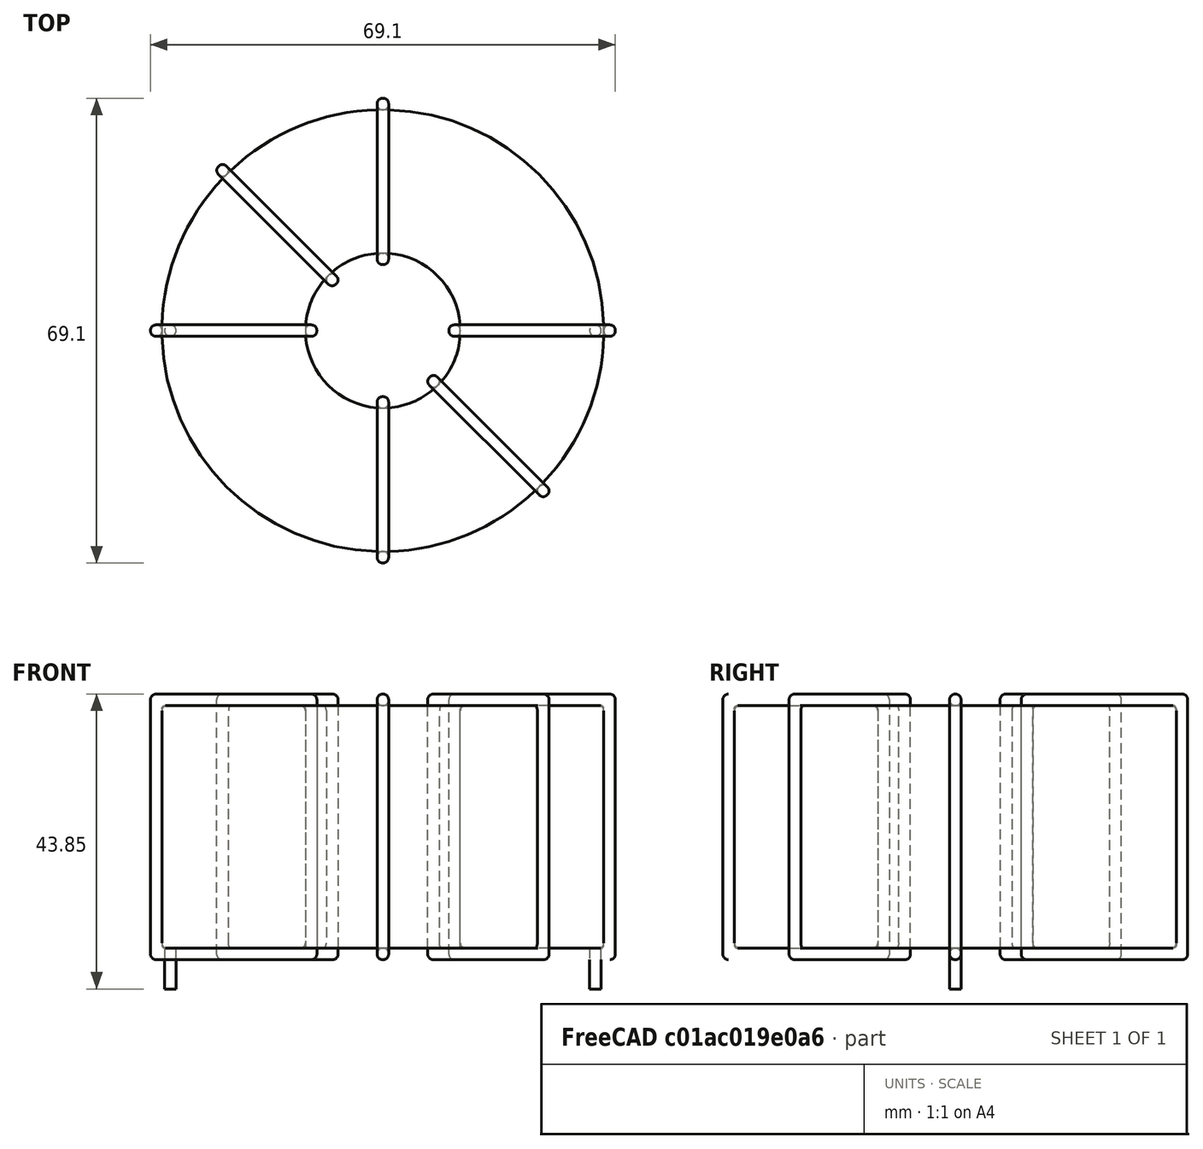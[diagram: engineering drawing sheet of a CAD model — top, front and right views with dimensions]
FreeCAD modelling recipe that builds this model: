
FCSTD DOCUMENT  (FreeCAD 0.16R6703 (Git))
Label: L_Toroid_Horizontal_D69.1mm_P63.20mm_Vishay_TJ9
License: All rights reserved
LicenseURL: http://en.wikipedia.org/wiki/All_rights_reserved
objects: Sketcher::SketchObject×6, PartDesign::Pad×6, PartDesign::Fillet×5, Spreadsheet::Sheet×1
note: 23 computed .brp shape members not serialized (recipe doc carries the construction recipe); baked Part::Feature solids carry a one-line shape summary decoded from their .brp

FEATURE [Spreadsheet::Sheet] Spreadsheet  label="dimensions"
  cells = A1=Wx; B1(Wx)=69.09999999999999; C1(WW)=23.03333333333333; D1=69.09999999999999; A2=Wy; B2(Wy)=69.09999999999999; D2=69.09999999999999; A3=RM; B3(RMx)=63.2; C3(RMy)=0; A4=d_wire; B4(d_wire)=1.7; A5=H; B5(H)=36.1; A6=offsetx; B6(offsetx)=2.949999999999996
FEATURE [Sketcher::SketchObject] Sketch
  Placement = pos=(0,0,2.2) rot=(0,0,1;0rad)
  expr: Placement.Base.z = 0.5 + Spreadsheet.d_wire
  expr: Constraints[0] = Spreadsheet.Wx / 2 - Spreadsheet.d_wire
  expr: Constraints[4] = Spreadsheet.WW / 2
  expr: Constraints[2] = Spreadsheet.RMy / 2
  expr: Constraints[1] = Spreadsheet.RMx / 2
  sketch-geometry (2):
    g0: Circle CenterX=31.6 CenterY=0 CenterZ=0 NormalX=0 NormalY=0 NormalZ=1 Radius=32.85
    g1: Circle CenterX=31.6 CenterY=0 CenterZ=0 NormalX=0 NormalY=0 NormalZ=1 Radius=11.5167
  constraints (5):
    c: Radius(g0) = 32.85
    c: DistanceX(g-1,g0) = 31.6
    c: DistanceY(g-1,g0) = 0
    c: Coincident(g1,g0)
    c: Radius(g1) = 11.5167
FEATURE [PartDesign::Pad] Pad
  Length = 36.1
  Length2 = 100
  Placement = pos=(0,0,2.2) rot=(0,0,1;0rad)
  Sketch = -> Sketch
  Type = 0
  expr: Length = Spreadsheet.H
FEATURE [Sketcher::SketchObject] Sketch001
  Placement = pos=(0,0,1.35) rot=(0,0,1;0rad)
  expr: Placement.Base.z = 0.5 + Spreadsheet.d_wire * 0.5
  expr: Constraints[4] = Spreadsheet.RMx
  expr: Constraints[2] = Spreadsheet.RMy
  expr: Constraints[1] = Spreadsheet.d_wire / 2
  sketch-geometry (2):
    g0: Circle CenterX=0 CenterY=0 CenterZ=0 NormalX=0 NormalY=0 NormalZ=1 Radius=0.85
    g1: Circle CenterX=63.2 CenterY=0 CenterZ=0 NormalX=0 NormalY=0 NormalZ=1 Radius=0.85
  constraints (5):
    c: Equal(g0,g1)
    c: Radius(g0) = 0.85
    c: DistanceY(g-1,g1) = 0
    c: Coincident(g0,g-1)
    c: DistanceX(g-1,g1) = 63.2
FEATURE [PartDesign::Pad] Pad001
  Length = 0.85
  Length2 = 5.2
  Placement = pos=(0,0,1.35) rot=(0,0,1;0rad)
  Reversed = true
  Sketch = -> Sketch001
  Type = 4
  expr: Length2 = 3.5 + Spreadsheet.d_wire
  expr: Length = Spreadsheet.d_wire / 2
FEATURE [PartDesign::Fillet] Fillet
  Base = -> Pad [Edge6,Edge3,Edge2]
  Placement = pos=(0,0,2.2) rot=(0,0,1;0rad)
  Radius = 0.5
FEATURE [Sketcher::SketchObject] Sketch003
  Placement = pos=(31.6,0,0) rot=(1,0,0;1.5708rad)
  expr: Placement.Base.x = Spreadsheet.RMx / 2
  expr: Constraints[49] = Spreadsheet.Wx - Spreadsheet.d_wire * 2
  expr: Constraints[44] = Spreadsheet.d_wire
  expr: Constraints[23] = Spreadsheet.H
  expr: Constraints[22] = Spreadsheet.Wx / 2 - Spreadsheet.d_wire
  expr: Placement.Base.y = Spreadsheet.RMy / 2
  expr: Constraints[21] = (Spreadsheet.Wx - Spreadsheet.WW) / 2 - Spreadsheet.d_wire
  expr: Constraints[19] = Spreadsheet.d_wire
  expr: Constraints[17] = Spreadsheet.d_wire
  expr: Constraints[18] = Spreadsheet.d_wire
  expr: Constraints[16] = Spreadsheet.d_wire
  sketch-geometry (16):
    g0: LineSegment StartX=-9.81667 StartY=0.5 StartZ=0 EndX=-34.55 EndY=0.5 EndZ=0
    g1: LineSegment StartX=-34.55 StartY=0.5 StartZ=0 EndX=-34.55 EndY=40 EndZ=0
    g2: LineSegment StartX=-34.55 StartY=40 StartZ=0 EndX=-9.81667 EndY=40 EndZ=0
    g3: LineSegment StartX=-9.81667 StartY=40 StartZ=0 EndX=-9.81667 EndY=0.5 EndZ=0
    g4: LineSegment StartX=-32.85 StartY=38.3 StartZ=0 EndX=-11.5167 EndY=38.3 EndZ=0
    g5: LineSegment StartX=-11.5167 StartY=38.3 StartZ=0 EndX=-11.5167 EndY=2.2 EndZ=0
    g6: LineSegment StartX=-11.5167 StartY=2.2 StartZ=0 EndX=-32.85 EndY=2.2 EndZ=0
    g7: LineSegment StartX=-32.85 StartY=2.2 StartZ=0 EndX=-32.85 EndY=38.3 EndZ=0
    g8: LineSegment StartX=9.81667 StartY=40 StartZ=0 EndX=34.55 EndY=40 EndZ=0
    g9: LineSegment StartX=34.55 StartY=40 StartZ=0 EndX=34.55 EndY=0.5 EndZ=0
    g10: LineSegment StartX=34.55 StartY=0.5 StartZ=0 EndX=9.81667 EndY=0.5 EndZ=0
    g11: LineSegment StartX=9.81667 StartY=0.5 StartZ=0 EndX=9.81667 EndY=40 EndZ=0
    g12: LineSegment StartX=11.5167 StartY=38.3 StartZ=0 EndX=32.85 EndY=38.3 EndZ=0
    g13: LineSegment StartX=32.85 StartY=38.3 StartZ=0 EndX=32.85 EndY=2.2 EndZ=0
    g14: LineSegment StartX=32.85 StartY=2.2 StartZ=0 EndX=11.5167 EndY=2.2 EndZ=0
    g15: LineSegment StartX=11.5167 StartY=2.2 StartZ=0 EndX=11.5167 EndY=38.3 EndZ=0
  constraints (50):
    c: Horizontal(g0)
    c: Coincident(g1,g0)
    c: Vertical(g1)
    c: Coincident(g2,g1)
    c: Horizontal(g2)
    c: Coincident(g3,g2)
    c: Coincident(g3,g0)
    c: Vertical(g3)
    c: Coincident(g4,g5)
    c: Coincident(g5,g6)
    c: Coincident(g6,g7)
    c: Coincident(g7,g4)
    c: Horizontal(g4)
    c: Horizontal(g6)
    c: Vertical(g5)
    c: Vertical(g7)
    c: DistanceX(g1,g4) = 1.7
    c: DistanceY(g4,g1) = 1.7
    c: DistanceX(g5,g0) = 1.7
    c: DistanceY(g0,g5) = 1.7
    c: DistanceY(g-1,g0) = 0.5
    c: DistanceX(g6,g6) = 21.3333
    c: DistanceX(g6,g-1) = 32.85
    c: DistanceY(g7,g7) = 36.1
    c: Coincident(g8,g9)
    c: Coincident(g9,g10)
    c: Coincident(g10,g11)
    c: Coincident(g11,g8)
    c: Horizontal(g8)
    c: Horizontal(g10)
    c: Vertical(g9)
    c: Vertical(g11)
    c: Coincident(g12,g13)
    c: Coincident(g13,g14)
    c: Coincident(g14,g15)
    c: Coincident(g15,g12)
    c: Horizontal(g12)
    c: Horizontal(g14)
    c: Vertical(g13)
    c: Vertical(g15)
    c: DistanceY(g8,g2) = 0
    c: DistanceY(g10,g0) = 0
    c: DistanceY(g14,g5) = 0
    c: DistanceY(g12,g4) = 0
    c: DistanceX(g8,g12) = 1.7
    c: Equal(g8,g2)
    c: Equal(g12,g4)
    c: Equal(g9,g1)
    c: Equal(g13,g7)
    c: DistanceX(g4,g12) = 65.7
FEATURE [PartDesign::Pad] Pad002
  Length = 1.7
  Length2 = 100
  Midplane = true
  Placement = pos=(31.6,0,0) rot=(1,0,0;1.5708rad)
  Sketch = -> Sketch003
  Type = 0
  expr: Length = Spreadsheet.d_wire
FEATURE [PartDesign::Fillet] Fillet001
  Base = -> Pad002 [Edge38,Edge41,Edge42,Edge43,Edge29,Edge32,Edge33,Edge34,Edge25,Edge35,Edge36,Edge13,Edge14,Edge15,Edge16,Edge17,Edge18,Edge19,Edge1,Edge2,Edge3,Edge4,Edge5,Edge6,Edge7,Edge37,Edge39,Edge40,Edge20,Edge23,Edge24,Edge21,Edge22,Edge8,Edge9,Edge10,Edge11,Edge12,Edge26,Edge27,+8 more]
  Placement = pos=(31.6,0,0) rot=(1,0,0;1.5708rad)
  Radius = 0.799
  expr: Radius = Spreadsheet.d_wire * 0.47
FEATURE [Sketcher::SketchObject] Sketch004
  Placement = pos=(31.6,0,0) rot=(0.862856,0.357407,0.357407;1.71777rad)
  expr: Placement.Base.x = Spreadsheet.RMx / 2
  expr: Constraints[49] = Spreadsheet.Wx - 2 * Spreadsheet.d_wire
  expr: Constraints[44] = Spreadsheet.d_wire
  expr: Constraints[23] = Spreadsheet.H
  expr: Constraints[22] = Spreadsheet.Wx / 2 - Spreadsheet.d_wire
  expr: Placement.Base.y = Spreadsheet.RMy / 2
  expr: Constraints[21] = (Spreadsheet.Wx - Spreadsheet.WW) / 2 - Spreadsheet.d_wire
  expr: Constraints[19] = Spreadsheet.d_wire
  expr: Constraints[17] = Spreadsheet.d_wire
  expr: Constraints[18] = Spreadsheet.d_wire
  expr: Constraints[16] = Spreadsheet.d_wire
  sketch-geometry (16):
    g0: LineSegment StartX=-9.81667 StartY=0.5 StartZ=0 EndX=-34.55 EndY=0.5 EndZ=0
    g1: LineSegment StartX=-34.55 StartY=0.5 StartZ=0 EndX=-34.55 EndY=40 EndZ=0
    g2: LineSegment StartX=-34.55 StartY=40 StartZ=0 EndX=-9.81667 EndY=40 EndZ=0
    g3: LineSegment StartX=-9.81667 StartY=40 StartZ=0 EndX=-9.81667 EndY=0.5 EndZ=0
    g4: LineSegment StartX=-32.85 StartY=38.3 StartZ=0 EndX=-11.5167 EndY=38.3 EndZ=0
    g5: LineSegment StartX=-11.5167 StartY=38.3 StartZ=0 EndX=-11.5167 EndY=2.2 EndZ=0
    g6: LineSegment StartX=-11.5167 StartY=2.2 StartZ=0 EndX=-32.85 EndY=2.2 EndZ=0
    g7: LineSegment StartX=-32.85 StartY=2.2 StartZ=0 EndX=-32.85 EndY=38.3 EndZ=0
    g8: LineSegment StartX=9.81667 StartY=40 StartZ=0 EndX=34.55 EndY=40 EndZ=0
    g9: LineSegment StartX=34.55 StartY=40 StartZ=0 EndX=34.55 EndY=0.5 EndZ=0
    g10: LineSegment StartX=34.55 StartY=0.5 StartZ=0 EndX=9.81667 EndY=0.5 EndZ=0
    g11: LineSegment StartX=9.81667 StartY=0.5 StartZ=0 EndX=9.81667 EndY=40 EndZ=0
    g12: LineSegment StartX=11.5167 StartY=38.3 StartZ=0 EndX=32.85 EndY=38.3 EndZ=0
    g13: LineSegment StartX=32.85 StartY=38.3 StartZ=0 EndX=32.85 EndY=2.2 EndZ=0
    g14: LineSegment StartX=32.85 StartY=2.2 StartZ=0 EndX=11.5167 EndY=2.2 EndZ=0
    g15: LineSegment StartX=11.5167 StartY=2.2 StartZ=0 EndX=11.5167 EndY=38.3 EndZ=0
  constraints (50):
    c: Horizontal(g0)
    c: Coincident(g1,g0)
    c: Vertical(g1)
    c: Coincident(g2,g1)
    c: Horizontal(g2)
    c: Coincident(g3,g2)
    c: Coincident(g3,g0)
    c: Vertical(g3)
    c: Coincident(g4,g5)
    c: Coincident(g5,g6)
    c: Coincident(g6,g7)
    c: Coincident(g7,g4)
    c: Horizontal(g4)
    c: Horizontal(g6)
    c: Vertical(g5)
    c: Vertical(g7)
    c: DistanceX(g1,g4) = 1.7
    c: DistanceY(g4,g1) = 1.7
    c: DistanceX(g5,g0) = 1.7
    c: DistanceY(g0,g5) = 1.7
    c: DistanceY(g-1,g0) = 0.5
    c: DistanceX(g6,g6) = 21.3333
    c: DistanceX(g6,g-1) = 32.85
    c: DistanceY(g7,g7) = 36.1
    c: Coincident(g8,g9)
    c: Coincident(g9,g10)
    c: Coincident(g10,g11)
    c: Coincident(g11,g8)
    c: Horizontal(g8)
    c: Horizontal(g10)
    c: Vertical(g9)
    c: Vertical(g11)
    c: Coincident(g12,g13)
    c: Coincident(g13,g14)
    c: Coincident(g14,g15)
    c: Coincident(g15,g12)
    c: Horizontal(g12)
    c: Horizontal(g14)
    c: Vertical(g13)
    c: Vertical(g15)
    c: DistanceY(g8,g2) = 0
    c: DistanceY(g10,g0) = 0
    c: DistanceY(g14,g5) = 0
    c: DistanceY(g12,g4) = 0
    c: DistanceX(g8,g12) = 1.7
    c: Equal(g8,g2)
    c: Equal(g12,g4)
    c: Equal(g9,g1)
    c: Equal(g13,g7)
    c: DistanceX(g4,g12) = 65.7
FEATURE [PartDesign::Pad] Pad003
  Length = 1.7
  Length2 = 100
  Midplane = true
  Placement = pos=(31.6,0,0) rot=(0.862856,0.357407,0.357407;1.71777rad)
  Sketch = -> Sketch004
  Type = 0
  expr: Length = Spreadsheet.d_wire
FEATURE [PartDesign::Fillet] Fillet002
  Base = -> Pad003 [Edge38,Edge41,Edge42,Edge43,Edge29,Edge32,Edge33,Edge34,Edge25,Edge35,Edge36,Edge13,Edge14,Edge15,Edge16,Edge17,Edge18,Edge19,Edge1,Edge2,Edge3,Edge4,Edge5,Edge6,Edge7,Edge37,Edge39,Edge40,Edge20,Edge23,Edge24,Edge21,Edge22,Edge8,Edge9,Edge10,Edge11,Edge12,Edge26,Edge27,+8 more]
  Placement = pos=(31.6,0,0) rot=(0.862856,0.357407,0.357407;1.71777rad)
  Radius = 0.799
  expr: Radius = Spreadsheet.d_wire * 0.47
FEATURE [Sketcher::SketchObject] Sketch005
  Placement = pos=(31.6,0,0) rot=(0.862856,-0.357407,-0.357407;1.71777rad)
  expr: Placement.Base.x = Spreadsheet.RMx / 2
  expr: Constraints[49] = Spreadsheet.Wx - 2 * Spreadsheet.d_wire
  expr: Constraints[44] = Spreadsheet.d_wire
  expr: Constraints[23] = Spreadsheet.H
  expr: Constraints[22] = Spreadsheet.Wx / 2 - Spreadsheet.d_wire
  expr: Placement.Base.y = Spreadsheet.RMy / 2
  expr: Constraints[21] = (Spreadsheet.Wx - Spreadsheet.WW) / 2 - Spreadsheet.d_wire
  expr: Constraints[19] = Spreadsheet.d_wire
  expr: Constraints[17] = Spreadsheet.d_wire
  expr: Constraints[18] = Spreadsheet.d_wire
  expr: Constraints[16] = Spreadsheet.d_wire
  sketch-geometry (16):
    g0: LineSegment StartX=-9.81667 StartY=0.5 StartZ=0 EndX=-34.55 EndY=0.5 EndZ=0
    g1: LineSegment StartX=-34.55 StartY=0.5 StartZ=0 EndX=-34.55 EndY=40 EndZ=0
    g2: LineSegment StartX=-34.55 StartY=40 StartZ=0 EndX=-9.81667 EndY=40 EndZ=0
    g3: LineSegment StartX=-9.81667 StartY=40 StartZ=0 EndX=-9.81667 EndY=0.5 EndZ=0
    g4: LineSegment StartX=-32.85 StartY=38.3 StartZ=0 EndX=-11.5167 EndY=38.3 EndZ=0
    g5: LineSegment StartX=-11.5167 StartY=38.3 StartZ=0 EndX=-11.5167 EndY=2.2 EndZ=0
    g6: LineSegment StartX=-11.5167 StartY=2.2 StartZ=0 EndX=-32.85 EndY=2.2 EndZ=0
    g7: LineSegment StartX=-32.85 StartY=2.2 StartZ=0 EndX=-32.85 EndY=38.3 EndZ=0
    g8: LineSegment StartX=9.81667 StartY=40 StartZ=0 EndX=34.55 EndY=40 EndZ=0
    g9: LineSegment StartX=34.55 StartY=40 StartZ=0 EndX=34.55 EndY=0.5 EndZ=0
    g10: LineSegment StartX=34.55 StartY=0.5 StartZ=0 EndX=9.81667 EndY=0.5 EndZ=0
    g11: LineSegment StartX=9.81667 StartY=0.5 StartZ=0 EndX=9.81667 EndY=40 EndZ=0
    g12: LineSegment StartX=11.5167 StartY=38.3 StartZ=0 EndX=32.85 EndY=38.3 EndZ=0
    g13: LineSegment StartX=32.85 StartY=38.3 StartZ=0 EndX=32.85 EndY=2.2 EndZ=0
    g14: LineSegment StartX=32.85 StartY=2.2 StartZ=0 EndX=11.5167 EndY=2.2 EndZ=0
    g15: LineSegment StartX=11.5167 StartY=2.2 StartZ=0 EndX=11.5167 EndY=38.3 EndZ=0
  constraints (50):
    c: Horizontal(g0)
    c: Coincident(g1,g0)
    c: Vertical(g1)
    c: Coincident(g2,g1)
    c: Horizontal(g2)
    c: Coincident(g3,g2)
    c: Coincident(g3,g0)
    c: Vertical(g3)
    c: Coincident(g4,g5)
    c: Coincident(g5,g6)
    c: Coincident(g6,g7)
    c: Coincident(g7,g4)
    c: Horizontal(g4)
    c: Horizontal(g6)
    c: Vertical(g5)
    c: Vertical(g7)
    c: DistanceX(g1,g4) = 1.7
    c: DistanceY(g4,g1) = 1.7
    c: DistanceX(g5,g0) = 1.7
    c: DistanceY(g0,g5) = 1.7
    c: DistanceY(g-1,g0) = 0.5
    c: DistanceX(g6,g6) = 21.3333
    c: DistanceX(g6,g-1) = 32.85
    c: DistanceY(g7,g7) = 36.1
    c: Coincident(g8,g9)
    c: Coincident(g9,g10)
    c: Coincident(g10,g11)
    c: Coincident(g11,g8)
    c: Horizontal(g8)
    c: Horizontal(g10)
    c: Vertical(g9)
    c: Vertical(g11)
    c: Coincident(g12,g13)
    c: Coincident(g13,g14)
    c: Coincident(g14,g15)
    c: Coincident(g15,g12)
    c: Horizontal(g12)
    c: Horizontal(g14)
    c: Vertical(g13)
    c: Vertical(g15)
    c: DistanceY(g8,g2) = 0
    c: DistanceY(g10,g0) = 0
    c: DistanceY(g14,g5) = 0
    c: DistanceY(g12,g4) = 0
    c: DistanceX(g8,g12) = 1.7
    c: Equal(g8,g2)
    c: Equal(g12,g4)
    c: Equal(g9,g1)
    c: Equal(g13,g7)
    c: DistanceX(g4,g12) = 65.7
FEATURE [PartDesign::Pad] Pad004
  Length = 1.7
  Length2 = 100
  Midplane = true
  Placement = pos=(31.6,0,0) rot=(0.862856,-0.357407,-0.357407;1.71777rad)
  Sketch = -> Sketch005
  Type = 0
  expr: Length = Spreadsheet.d_wire
FEATURE [PartDesign::Fillet] Fillet003
  Base = -> Pad004 [Edge38,Edge41,Edge42,Edge43,Edge29,Edge32,Edge33,Edge34,Edge25,Edge35,Edge36,Edge13,Edge14,Edge15,Edge16,Edge17,Edge18,Edge19,Edge1,Edge2,Edge3,Edge4,Edge5,Edge6,Edge7,Edge37,Edge39,Edge40,Edge20,Edge23,Edge24,Edge21,Edge22,Edge8,Edge9,Edge10,Edge11,Edge12,Edge26,Edge27,+8 more]
  Placement = pos=(31.6,0,0) rot=(0.862856,-0.357407,-0.357407;1.71777rad)
  Radius = 0.799
  expr: Radius = Spreadsheet.d_wire * 0.47
FEATURE [Sketcher::SketchObject] Sketch006
  Placement = pos=(31.6,0,0) rot=(0.57735,0.57735,0.57735;2.0944rad)
  expr: Placement.Base.x = Spreadsheet.RMx / 2
  expr: Constraints[49] = Spreadsheet.Wx - Spreadsheet.d_wire * 2
  expr: Constraints[44] = Spreadsheet.d_wire
  expr: Constraints[23] = Spreadsheet.H
  expr: Constraints[22] = Spreadsheet.Wx / 2 - Spreadsheet.d_wire
  expr: Placement.Base.y = Spreadsheet.RMy / 2
  expr: Constraints[21] = (Spreadsheet.Wx - Spreadsheet.WW) / 2 - Spreadsheet.d_wire
  expr: Constraints[19] = Spreadsheet.d_wire
  expr: Constraints[17] = Spreadsheet.d_wire
  expr: Constraints[18] = Spreadsheet.d_wire
  expr: Constraints[16] = Spreadsheet.d_wire
  sketch-geometry (16):
    g0: LineSegment StartX=-9.81667 StartY=0.5 StartZ=0 EndX=-34.55 EndY=0.5 EndZ=0
    g1: LineSegment StartX=-34.55 StartY=0.5 StartZ=0 EndX=-34.55 EndY=40 EndZ=0
    g2: LineSegment StartX=-34.55 StartY=40 StartZ=0 EndX=-9.81667 EndY=40 EndZ=0
    g3: LineSegment StartX=-9.81667 StartY=40 StartZ=0 EndX=-9.81667 EndY=0.5 EndZ=0
    g4: LineSegment StartX=-32.85 StartY=38.3 StartZ=0 EndX=-11.5167 EndY=38.3 EndZ=0
    g5: LineSegment StartX=-11.5167 StartY=38.3 StartZ=0 EndX=-11.5167 EndY=2.2 EndZ=0
    g6: LineSegment StartX=-11.5167 StartY=2.2 StartZ=0 EndX=-32.85 EndY=2.2 EndZ=0
    g7: LineSegment StartX=-32.85 StartY=2.2 StartZ=0 EndX=-32.85 EndY=38.3 EndZ=0
    g8: LineSegment StartX=9.81667 StartY=40 StartZ=0 EndX=34.55 EndY=40 EndZ=0
    g9: LineSegment StartX=34.55 StartY=40 StartZ=0 EndX=34.55 EndY=0.5 EndZ=0
    g10: LineSegment StartX=34.55 StartY=0.5 StartZ=0 EndX=9.81667 EndY=0.5 EndZ=0
    g11: LineSegment StartX=9.81667 StartY=0.5 StartZ=0 EndX=9.81667 EndY=40 EndZ=0
    g12: LineSegment StartX=11.5167 StartY=38.3 StartZ=0 EndX=32.85 EndY=38.3 EndZ=0
    g13: LineSegment StartX=32.85 StartY=38.3 StartZ=0 EndX=32.85 EndY=2.2 EndZ=0
    g14: LineSegment StartX=32.85 StartY=2.2 StartZ=0 EndX=11.5167 EndY=2.2 EndZ=0
    g15: LineSegment StartX=11.5167 StartY=2.2 StartZ=0 EndX=11.5167 EndY=38.3 EndZ=0
  constraints (50):
    c: Horizontal(g0)
    c: Coincident(g1,g0)
    c: Vertical(g1)
    c: Coincident(g2,g1)
    c: Horizontal(g2)
    c: Coincident(g3,g2)
    c: Coincident(g3,g0)
    c: Vertical(g3)
    c: Coincident(g4,g5)
    c: Coincident(g5,g6)
    c: Coincident(g6,g7)
    c: Coincident(g7,g4)
    c: Horizontal(g4)
    c: Horizontal(g6)
    c: Vertical(g5)
    c: Vertical(g7)
    c: DistanceX(g1,g4) = 1.7
    c: DistanceY(g4,g1) = 1.7
    c: DistanceX(g5,g0) = 1.7
    c: DistanceY(g0,g5) = 1.7
    c: DistanceY(g-1,g0) = 0.5
    c: DistanceX(g6,g6) = 21.3333
    c: DistanceX(g6,g-1) = 32.85
    c: DistanceY(g7,g7) = 36.1
    c: Coincident(g8,g9)
    c: Coincident(g9,g10)
    c: Coincident(g10,g11)
    c: Coincident(g11,g8)
    c: Horizontal(g8)
    c: Horizontal(g10)
    c: Vertical(g9)
    c: Vertical(g11)
    c: Coincident(g12,g13)
    c: Coincident(g13,g14)
    c: Coincident(g14,g15)
    c: Coincident(g15,g12)
    c: Horizontal(g12)
    c: Horizontal(g14)
    c: Vertical(g13)
    c: Vertical(g15)
    c: DistanceY(g8,g2) = 0
    c: DistanceY(g10,g0) = 0
    c: DistanceY(g14,g5) = 0
    c: DistanceY(g12,g4) = 0
    c: DistanceX(g8,g12) = 1.7
    c: Equal(g8,g2)
    c: Equal(g12,g4)
    c: Equal(g9,g1)
    c: Equal(g13,g7)
    c: DistanceX(g4,g12) = 65.7
FEATURE [PartDesign::Pad] Pad005
  Length = 1.7
  Length2 = 100
  Midplane = true
  Placement = pos=(31.6,0,0) rot=(0.57735,0.57735,0.57735;2.0944rad)
  Sketch = -> Sketch006
  Type = 0
  expr: Length = Spreadsheet.d_wire
FEATURE [PartDesign::Fillet] Fillet004
  Base = -> Pad005 [Edge38,Edge41,Edge42,Edge43,Edge29,Edge32,Edge33,Edge34,Edge25,Edge35,Edge36,Edge13,Edge14,Edge15,Edge16,Edge17,Edge18,Edge19,Edge1,Edge2,Edge3,Edge4,Edge5,Edge6,Edge7,Edge37,Edge39,Edge40,Edge20,Edge23,Edge24,Edge21,Edge22,Edge8,Edge9,Edge10,Edge11,Edge12,Edge26,Edge27,+8 more]
  Placement = pos=(31.6,0,0) rot=(0.57735,0.57735,0.57735;2.0944rad)
  Radius = 0.799
  expr: Radius = Spreadsheet.d_wire * 0.47
